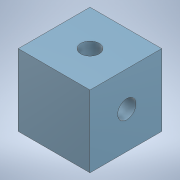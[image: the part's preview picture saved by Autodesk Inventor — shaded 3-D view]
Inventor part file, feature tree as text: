
AUTODESK INVENTOR PART (.ipt)
format: ipt  version: 2022 (Build 260153000, 153)  size: 139,264 bytes
history: native  units: mm
features: sketch x4, extrude x2, hole x1
ambient origin geometry x8: Origin, YZ Plane, XZ Plane, XY Plane, X Axis, Y Axis, Z Axis, Center Point
bodies: Solid1 (feature_tree), Body (feature_tree)
feature tree (7):
  extrude  "RotAxis"  Depth=156.0mm
  extrude  "CableHole"  TaperAngle=0.0deg  [1 undecoded]
  hole  "BoltHoles"  [1 undecoded]
  sketch  "Sketch1"  dims[d0=156.0mm d1=156.0mm]
  sketch  "Sketch2"  dims[d2=156.0mm d3=0.0mm d4=0.0mm d5=0.0mm]
  sketch  "Sketch4"  dims[d8=0.0mm d9=0.0mm]
  sketch  "Sketch5"  dims[d10=6.0mm d11=12.7mm d12=3.023mm d13=2.0mm d14=14.3117mm d15=20.0mm d16=20.594885mm]
note: 2 required parameter values undecoded (feature->parameter linkage not recoverable at this tier; creation-order binding heuristic only, values carry confidence <= 0.55)
